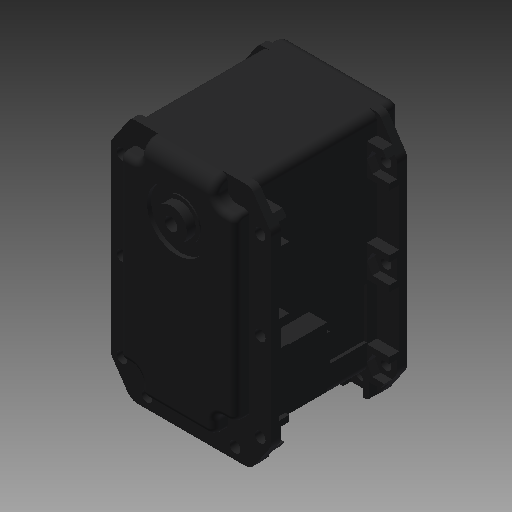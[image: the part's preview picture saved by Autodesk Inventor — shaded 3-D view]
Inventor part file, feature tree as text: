
AUTODESK INVENTOR PART (.ipt)
format: ipt  version: 2019 (Build 230136000, 136)  size: 711,168 bytes
history: native  units: in
note: dims shown in document units (in); Inventor stores cm internally (conversion verified against a paired STEP export)
features: other x3, sketch x3
ambient origin geometry x8: Origin, YZ Plane, XZ Plane, XY Plane, X Axis, Y Axis, Z Axis, Center Point
bodies: Solid1 (feature_tree)
feature tree (6):
  other  "MX-64T.ipt"
  other  "Solid1::MX-64T.ipt"
  other  "TaggingFeature1"
  sketch  "Sketch1"  dims[d0=0.3937in]
  sketch  "Sketch2"  dims[d2=0.1575in d3=0.0in d4=0.0in]
  sketch  "Sketch3"
